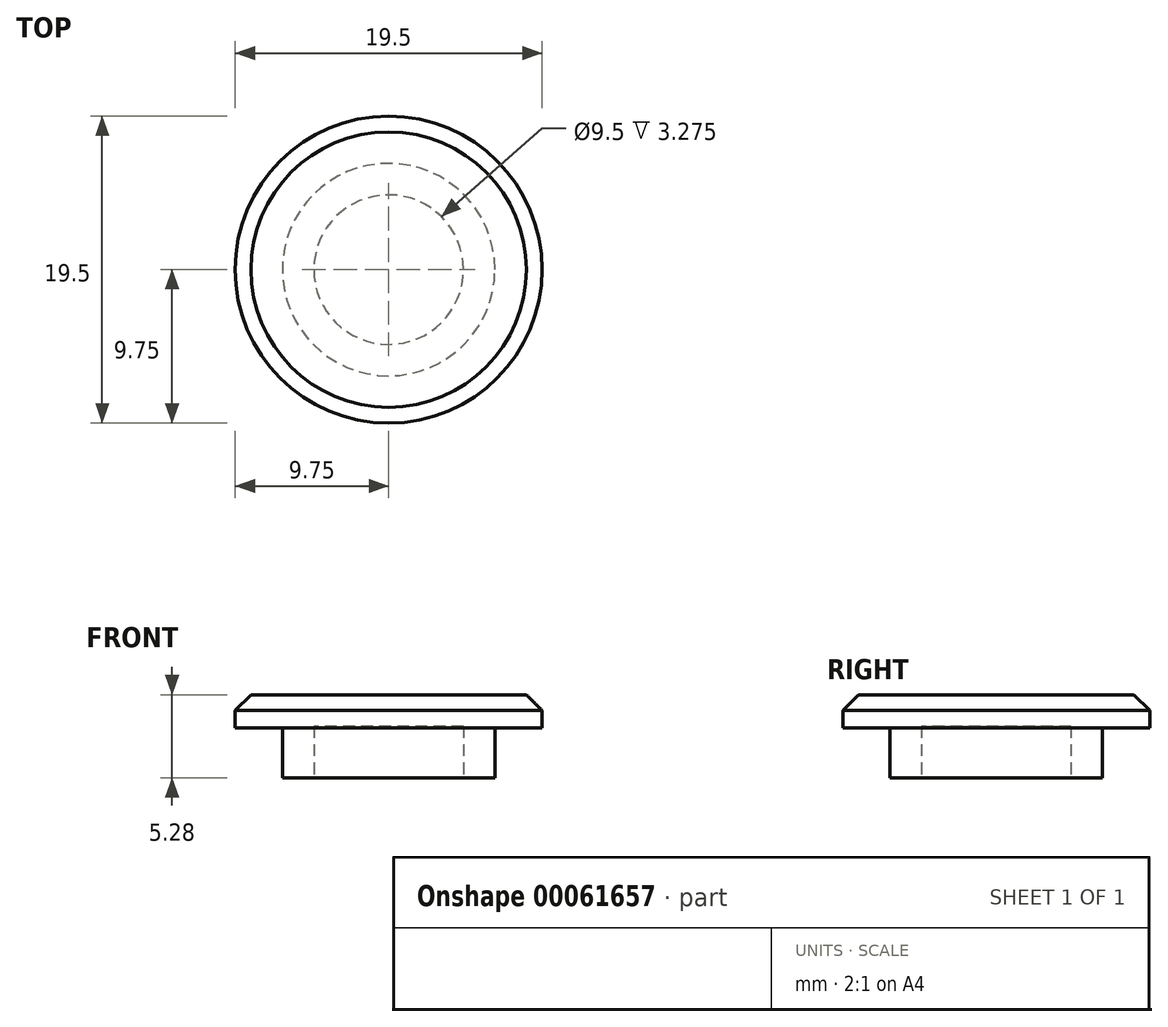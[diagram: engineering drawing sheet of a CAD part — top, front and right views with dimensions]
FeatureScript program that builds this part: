
annotation { "Feature Type Name" : "Feature", "Feature Type Description" : "" }
export const myFeature = defineFeature(function(context is Context, id is Id, definition is map)
    precondition{}
    {
        {
            var Q0;
            Q0=qCreatedBy(makeId("Top.planeOp"),FACE);
            var sketch = newSketch(context, id + "F0", { "sketchPlane" : qUnion([Q0])});
            skCircle(sketch, "E0", {"center": v(0, 0) * mm, "radius": 6.75 * mm});
            skSolve(sketch);
        }
        {
            var Q0;
            Q0 = qSketchRegion(id + "F0", true);
            extrude(context, id + "F1", {"entities" : qUnion([Q0]), "depth" : 3.17 * mm});
        }
        {
            var Q0;
            Q0=makeQuery(id+"F1.opExtrude","CAP_FACE",FACE,{"disambiguationData":[OSD([sQuery(id+"F0.wireOp",EDGE,"E0")])],"isStart":false});
            var sketch = newSketch(context, id + "F2", { "sketchPlane" : qUnion([Q0])});
            skCircle(sketch, "E1", {"center": v(0, 0) * mm, "radius": 9.75 * mm});
            skSolve(sketch);
        }
        {
            var Q0;
            Q0 = qSketchRegion(id + "F2", true);
            extrude(context, id + "F3", {"entities" : qUnion([Q0]), "operationType" : NewBodyOperationType.ADD, "depth" : 2.1 * mm});
        }
        {
            var Q0;
            Q0=makeQuery(id+"F3.opExtrude","CAP_EDGE",EDGE,{"disambiguationData":[OSD([sQuery(id+"F2.wireOp",EDGE,"E1")])],"isStart":false});
            chamfer(context, id + "F4", {"entities" : qUnion([Q0]), "width" : 1 * mm, "tangentPropagation" : true});
        }
        {
            var Q0;
            Q0=makeQuery(id+"F1.opExtrude","CAP_FACE",FACE,{"disambiguationData":[OSD([sQuery(id+"F0.wireOp",EDGE,"E0")])],"isStart":true});
            shell(context, id + "F5", {"entities" : qUnion([Q0]), "thickness" : 2 * mm});
        }
    });
